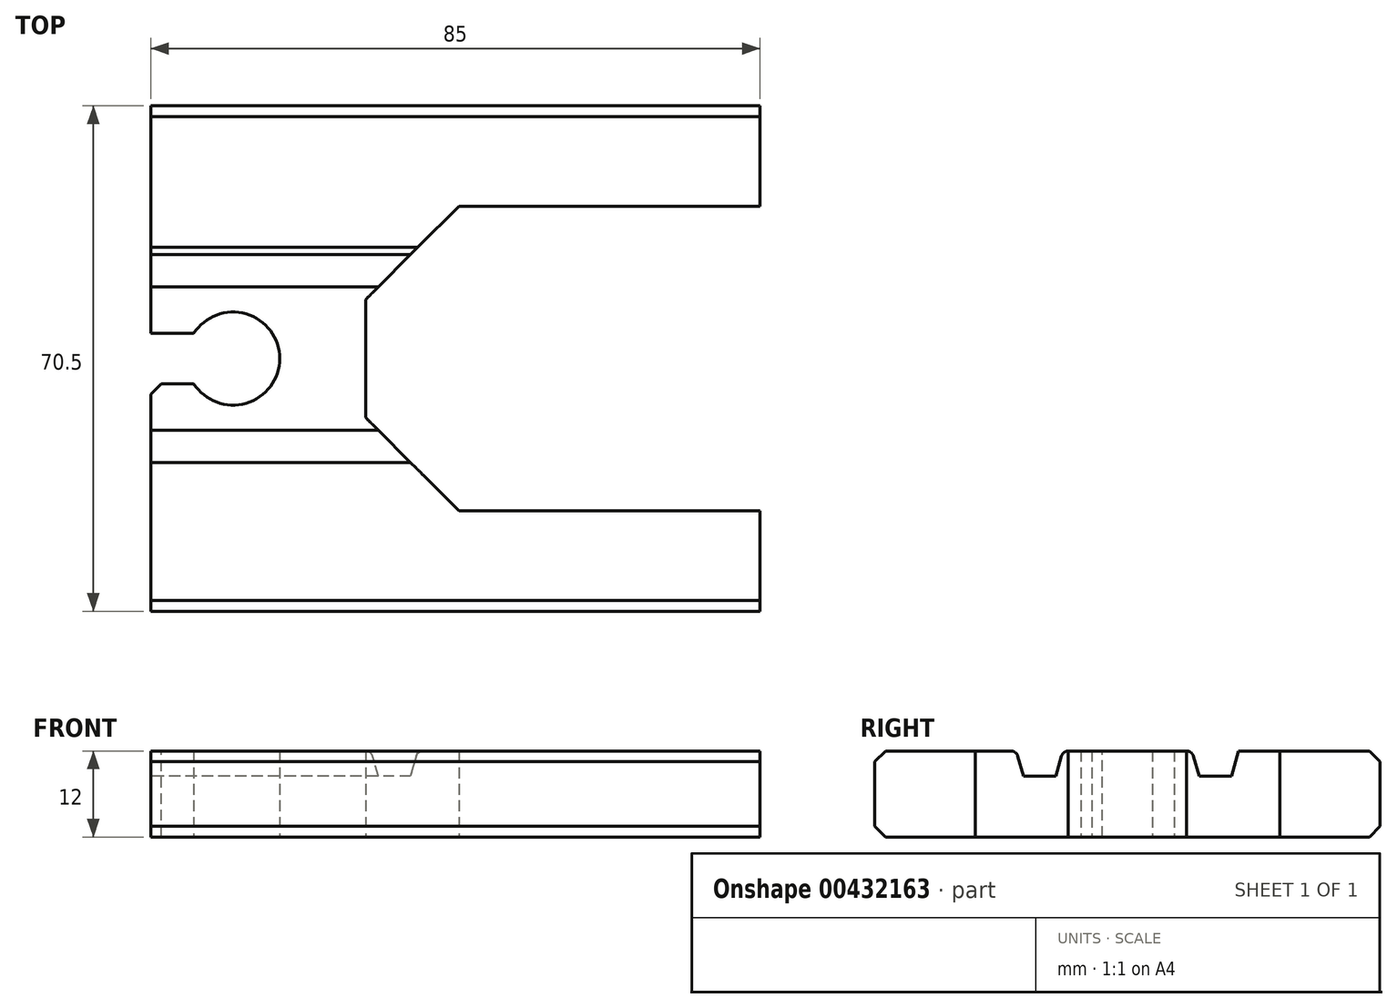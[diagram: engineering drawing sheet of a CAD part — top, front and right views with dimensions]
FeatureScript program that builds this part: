
annotation { "Feature Type Name" : "Feature", "Feature Type Description" : "" }
export const myFeature = defineFeature(function(context is Context, id is Id, definition is map)
    precondition{}
    {
        {
            var Q0;
            Q0=qCreatedBy(makeId("Top.planeOp"),FACE);
            var sketch = newSketch(context, id + "F0", { "sketchPlane" : qUnion([Q0])});
            skLineSegment(sketch, "E0", {"start": v(0, 35.25) * mm, "end": v(85, 35.25) * mm});
            skLineSegment(sketch, "E1", {"start": v(85, 35.25) * mm, "end": v(85, 21.25) * mm});
            skLineSegment(sketch, "E2", {"start": v(85, 21.25) * mm, "end": v(43, 21.25) * mm});
            skLineSegment(sketch, "E3", {"start": v(43, 21.25) * mm, "end": v(30, 8.25) * mm});
            skLineSegment(sketch, "E4", {"start": v(30, 8.25) * mm, "end": v(30, -8.25) * mm});
            skLineSegment(sketch, "E5", {"start": v(30, -8.25) * mm, "end": v(43, -21.25) * mm});
            skLineSegment(sketch, "E6", {"start": v(43, -21.25) * mm, "end": v(85, -21.25) * mm});
            skLineSegment(sketch, "E7", {"start": v(85, -21.25) * mm, "end": v(85, -35.25) * mm});
            skLineSegment(sketch, "E8", {"start": v(85, -35.25) * mm, "end": v(0, -35.25) * mm});
            skLineSegment(sketch, "E9", {"start": v(0, -35.25) * mm, "end": v(0, 35.25) * mm});
            skPoint(sketch, "E10", {"position": v(0, 0) * mm});
            skSolve(sketch);
        }
        {
            var Q0;
            Q0=makeQuery(id+"F0.imprint","IMPRINT",FACE,{"disambiguationData":[TD([[makeQuery(id+"F0.imprint","IMPRINT",EDGE,{"derivedFrom":sQuery(id+"F0.wireOp",EDGE,"E0")}),-1.0]])]});
            extrude(context, id + "F1", {"entities" : qUnion([Q0]), "depth" : 12 * mm});
        }
        {
            var Q0;
            Q0=qCreatedBy(makeId("Top.planeOp"),FACE);
            var sketch = newSketch(context, id + "F2", { "sketchPlane" : qUnion([Q0])});
            skLineSegment(sketch, "E11.bottom", {"start": v(0, 3.5) * mm, "end": v(8, 3.5) * mm});
            skLineSegment(sketch, "E11.top", {"start": v(0, -3.5) * mm, "end": v(8, -3.5) * mm});
            skLineSegment(sketch, "E11.left", {"start": v(0, 3.5) * mm, "end": v(0, -3.5) * mm});
            skLineSegment(sketch, "E11.right", {"start": v(8, 3.5) * mm, "end": v(8, -3.5) * mm});
            skSolve(sketch);
        }
        {
            var Q0;
            Q0 = qSketchRegion(id + "F2", true);
            extrude(context, id + "F3", {"entities" : qUnion([Q0]), "operationType" : NewBodyOperationType.REMOVE, "oppositeDirection" : true, "depth" : -12 * mm});
        }
        {
            var Q0;
            Q0=qCreatedBy(makeId("Top.planeOp"),FACE);
            var sketch = newSketch(context, id + "F4", { "sketchPlane" : qUnion([Q0])});
            skCircle(sketch, "E12", {"center": v(11.5, 0) * mm, "radius": 6.5 * mm});
            skSolve(sketch);
        }
        {
            var Q0;
            Q0 = qSketchRegion(id + "F4", true);
            extrude(context, id + "F5", {"entities" : qUnion([Q0]), "operationType" : NewBodyOperationType.REMOVE, "oppositeDirection" : true, "depth" : -12 * mm});
        }
        {
            var Q0;
            Q0=makeQuery(id+"F1.opExtrude","CAP_EDGE",EDGE,{"disambiguationData":[OSD([sQuery(id+"F0.wireOp",EDGE,"E8")])],"isStart":false});
            var Q1;
            Q1=makeQuery(id+"F1.opExtrude","CAP_EDGE",EDGE,{"disambiguationData":[OSD([sQuery(id+"F0.wireOp",EDGE,"E0")])],"isStart":false});
            var Q2;
            Q2=makeQuery(id+"F1.opExtrude","CAP_EDGE",EDGE,{"disambiguationData":[OSD([sQuery(id+"F0.wireOp",EDGE,"E8")])],"isStart":true});
            var Q3;
            Q3=makeQuery(id+"F1.opExtrude","CAP_EDGE",EDGE,{"disambiguationData":[OSD([sQuery(id+"F0.wireOp",EDGE,"E0")])],"isStart":true});
            var Q4;
            Q4=makeQuery(id+"F3.boolean.opBoolean","COPY",EDGE,{"derivedFrom":makeQuery(id+"F3.opExtrude","SWEPT_EDGE",EDGE,{"disambiguationData":[OSD([sQuery(id+"F2.wireOp",EDGE,"E11.bottom"),sQuery(id+"F2.wireOp",EDGE,"E11.left")])]})});
            var Q5;
            Q5=makeQuery(id+"F3.boolean.opBoolean","COPY",EDGE,{"derivedFrom":makeQuery(id+"F3.opExtrude","SWEPT_EDGE",EDGE,{"disambiguationData":[OSD([sQuery(id+"F2.wireOp",EDGE,"E11.top"),sQuery(id+"F2.wireOp",EDGE,"E11.left")])]})});
            chamfer(context, id + "F6", {"entities" : qUnion([Q0, Q1, Q2, Q3, Q4, Q5]), "width" : 1.5 * mm, "tangentPropagation" : true});
        }
        {
            var Q0;
            Q0=qCreatedBy(makeId("Right.planeOp"),FACE);
            var sketch = newSketch(context, id + "F7", { "sketchPlane" : qUnion([Q0])});
            skLineSegment(sketch, "E13", {"start": v(-9, 12) * mm, "end": v(-10, 8.5) * mm});
            skLineSegment(sketch, "E14", {"start": v(-10, 8.5) * mm, "end": v(-14.5, 8.5) * mm});
            skLineSegment(sketch, "E15", {"start": v(-14.5, 8.5) * mm, "end": v(-15.5, 12) * mm});
            skLineSegment(sketch, "E16", {"start": v(-9, 12) * mm, "end": v(-15.5, 12) * mm});
            skLineSegment(sketch, "E17", {"start": v(15.5, 12) * mm, "end": v(9, 12) * mm});
            skLineSegment(sketch, "E18", {"start": v(9, 12) * mm, "end": v(10, 8.5) * mm});
            skLineSegment(sketch, "E19", {"start": v(10, 8.5) * mm, "end": v(14.5, 8.5) * mm});
            skLineSegment(sketch, "E20", {"start": v(14.5, 8.5) * mm, "end": v(15.5, 12) * mm});
            skSolve(sketch);
        }
        {
            var Q0;
            Q0 = qSketchRegion(id + "F7", true);
            extrude(context, id + "F8", {"entities" : qUnion([Q0]), "operationType" : NewBodyOperationType.REMOVE, "oppositeDirection" : true, "depth" : -40 * mm});
        }
        {
            var Q0;
            Q0=makeQuery(id+"F8.boolean.opBoolean","COPY",EDGE,{"derivedFrom":makeQuery(id+"F8.opExtrude","SWEPT_EDGE",EDGE,{"disambiguationData":[OSD([sQuery(id+"F7.wireOp",EDGE,"E17"),sQuery(id+"F7.wireOp",EDGE,"E20")])]})});
            var Q1;
            Q1=makeQuery(id+"F8.boolean.opBoolean","COPY",EDGE,{"derivedFrom":makeQuery(id+"F8.opExtrude","SWEPT_EDGE",EDGE,{"disambiguationData":[OSD([sQuery(id+"F7.wireOp",EDGE,"E15"),sQuery(id+"F7.wireOp",EDGE,"E16")])]})});
            var Q2;
            Q2=makeQuery(id+"F8.boolean.opBoolean","COPY",EDGE,{"derivedFrom":makeQuery(id+"F8.opExtrude","SWEPT_EDGE",EDGE,{"disambiguationData":[OSD([sQuery(id+"F7.wireOp",EDGE,"E13"),sQuery(id+"F7.wireOp",EDGE,"E16")])]})});
            var Q3;
            Q3=makeQuery(id+"F8.boolean.opBoolean","COPY",EDGE,{"derivedFrom":makeQuery(id+"F8.opExtrude","SWEPT_EDGE",EDGE,{"disambiguationData":[OSD([sQuery(id+"F7.wireOp",EDGE,"E17"),sQuery(id+"F7.wireOp",EDGE,"E18")])]})});
            fillet(context, id + "F9", {"entities" : qUnion([Q0, Q1, Q2, Q3]), "radius" : 1 * mm, "tangentPropagation" : true, "allowEdgeOverflow" : false});
        }
    });
